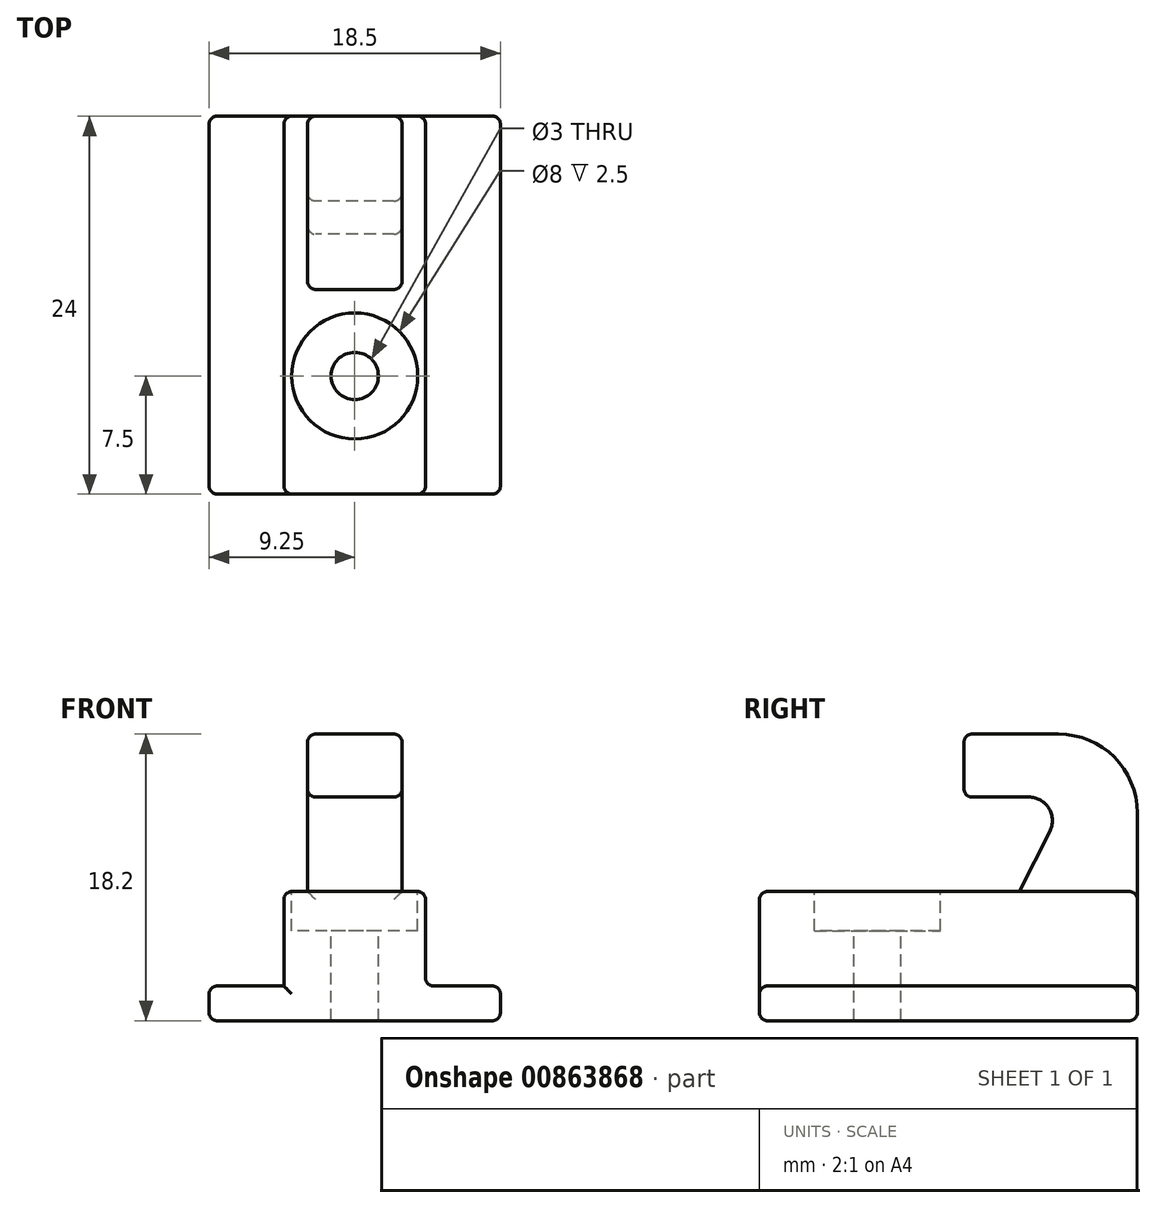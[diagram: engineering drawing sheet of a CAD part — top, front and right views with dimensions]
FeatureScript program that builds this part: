
annotation { "Feature Type Name" : "Feature", "Feature Type Description" : "" }
export const myFeature = defineFeature(function(context is Context, id is Id, definition is map)
    precondition{}
    {
        {
            var Q0;
            Q0=qCreatedBy(makeId("Top.planeOp"),FACE);
            var sketch = newSketch(context, id + "F0", { "sketchPlane" : qUnion([Q0])});
            skLineSegment(sketch, "E0.bottom", {"start": v(-9.25, 0) * mm, "end": v(9.25, 0) * mm});
            skLineSegment(sketch, "E0.top", {"start": v(-9.25, -24) * mm, "end": v(9.25, -24) * mm});
            skLineSegment(sketch, "E0.left", {"start": v(-9.25, 0) * mm, "end": v(-9.25, -24) * mm});
            skLineSegment(sketch, "E0.right", {"start": v(9.25, 0) * mm, "end": v(9.25, -24) * mm});
            skSolve(sketch);
        }
        {
            var Q0;
            Q0 = qSketchRegion(id + "F0", true);
            extrude(context, id + "F1", {"entities" : qUnion([Q0]), "depth" : 2.2 * mm, "offsetDistance" : 25 * mm});
        }
        {
            var Q0;
            Q0=makeQuery(id+"F1.opExtrude","CAP_FACE",FACE,{"disambiguationData":[OSD([sQuery(id+"F0.wireOp",EDGE,"E0.bottom"),sQuery(id+"F0.wireOp",EDGE,"E0.top"),sQuery(id+"F0.wireOp",EDGE,"E0.left"),sQuery(id+"F0.wireOp",EDGE,"E0.right")])],"isStart":false});
            var sketch = newSketch(context, id + "F2", { "sketchPlane" : qUnion([Q0])});
            skLineSegment(sketch, "E1.bottom", {"start": v(-4.5, 0) * mm, "end": v(4.5, 0) * mm});
            skLineSegment(sketch, "E1.top", {"start": v(-4.5, -24) * mm, "end": v(4.5, -24) * mm});
            skLineSegment(sketch, "E1.left", {"start": v(-4.5, 0) * mm, "end": v(-4.5, -24) * mm});
            skLineSegment(sketch, "E1.right", {"start": v(4.5, 0) * mm, "end": v(4.5, -24) * mm});
            skSolve(sketch);
        }
        {
            var Q0;
            Q0 = qSketchRegion(id + "F2", true);
            extrude(context, id + "F3", {"entities" : qUnion([Q0]), "operationType" : NewBodyOperationType.ADD, "depth" : 6 * mm, "offsetDistance" : 25 * mm});
        }
        {
            var Q0;
            Q0=qCreatedBy(makeId("Right.planeOp"),FACE);
            var sketch = newSketch(context, id + "F4", { "sketchPlane" : qUnion([Q0])});
            skLineSegment(sketch, "E2", {"start": v(-7.5, 8.2) * mm, "end": v(0, 8.2) * mm});
            skLineSegment(sketch, "E3", {"start": v(0, 8.2) * mm, "end": v(0, 17.51) * mm});
            skArc(sketch, "E4", {"start": v(0, 13.2) * mm, "mid": v(-1.46, 16.74) * mm, "end": v(-5, 18.2) * mm});
            skLineSegment(sketch, "E5", {"start": v(-7.5, 8.2) * mm, "end": v(-5.55, 12.02) * mm});
            skArc(sketch, "E6", {"start": v(-5.55, 12.02) * mm, "mid": v(-5.61, 13.48) * mm, "end": v(-6.9, 14.2) * mm});
            skLineSegment(sketch, "E7", {"start": v(-5, 18.58) * mm, "end": v(-5, 10.04) * mm, "construction": true});
            skLineSegment(sketch, "E8", {"start": v(-4.44, 18.2) * mm, "end": v(-10.5, 18.2) * mm});
            skLineSegment(sketch, "E9", {"start": v(-11, 17.7) * mm, "end": v(-11, 14.7) * mm});
            skLineSegment(sketch, "E10", {"start": v(-10.5, 14.2) * mm, "end": v(-6.9, 14.2) * mm});
            skPoint(sketch, "E11.visualSharp", {"position": v(-11, 18.2) * mm});
            skArc(sketch, "E11.filletArc", {"start": v(-10.5, 18.2) * mm, "mid": v(-10.85, 18.05) * mm, "end": v(-11, 17.7) * mm});
            skPoint(sketch, "E12.visualSharp", {"position": v(-11, 14.2) * mm});
            skArc(sketch, "E12.filletArc", {"start": v(-11, 14.7) * mm, "mid": v(-10.85, 14.35) * mm, "end": v(-10.5, 14.2) * mm});
            skSolve(sketch);
        }
        {
            var Q0;
            Q0 = qSketchRegion(id + "F4", true);
            extrude(context, id + "F5", {"entities" : qUnion([Q0]), "operationType" : NewBodyOperationType.ADD, "depth" : 3 * mm, "offsetDistance" : 25 * mm, "hasSecondDirection" : true, "secondDirectionOppositeDirection" : true, "secondDirectionDepth" : 3 * mm});
        }
        {
            var Q0;
            Q0=makeQuery(id+"F3.opExtrude","CAP_FACE",FACE,{"disambiguationData":[OSD([sQuery(id+"F2.wireOp",EDGE,"E1.bottom"),sQuery(id+"F2.wireOp",EDGE,"E1.top"),sQuery(id+"F2.wireOp",EDGE,"E1.left"),sQuery(id+"F2.wireOp",EDGE,"E1.right")])],"isStart":false});
            var sketch = newSketch(context, id + "F6", { "sketchPlane" : qUnion([Q0])});
            skPoint(sketch, "E13", {"position": v(0, -16.5) * mm});
            skSolve(sketch);
        }
        {
            var Q0;
            Q0=sQuery(id+"F6.wireOp",VERTEX,"E13");
            var Q1;
            Q1=makeQuery(id+"F1.opExtrude","SWEPT_BODY",BODY,{"disambiguationData":[OSD([sQuery(id+"F0.wireOp",EDGE,"E0.bottom"),sQuery(id+"F0.wireOp",EDGE,"E0.top"),sQuery(id+"F0.wireOp",EDGE,"E0.left"),sQuery(id+"F0.wireOp",EDGE,"E0.right")])]});
            hole(context, id + "F7", {"style" : HoleStyle.C_BORE, "endStyle" : HoleEndStyle.BLIND, "holeDiameter" : 3 * mm, "cBoreDiameter" : 8 * mm, "cBoreDepth" : 2.5 * mm, "majorDiameter" : 5 * mm, "holeDepth" : 15 * mm, "isTappedThrough" : true, "tappedDepth" : 12 * mm, "tapClearance" : 3, "startFromSketch" : true, "locations" : qUnion([Q0]), "scope" : qUnion([Q1])});
        }
        {
            var Q0;
            Q0=makeQuery(id+"F3.opExtrude","SWEPT_EDGE",EDGE,{"disambiguationData":[OSD([sQuery(id+"F0.wireOp",EDGE,"E0.top"),sQuery(id+"F2.wireOp",EDGE,"E1.top"),sQuery(id+"F2.wireOp",EDGE,"E1.left")])]});
            var Q1;
            Q1=makeQuery(id+"F1.opExtrude","SWEPT_EDGE",EDGE,{"disambiguationData":[OSD([sQuery(id+"F0.wireOp",EDGE,"E0.top"),sQuery(id+"F0.wireOp",EDGE,"E0.right")])]});
            var Q2;
            Q2=makeQuery(id+"F1.opExtrude","CAP_EDGE",EDGE,{"disambiguationData":[OSD([sQuery(id+"F0.wireOp",EDGE,"E0.left")])],"isStart":true});
            var Q3;
            Q3=makeQuery(id+"F1.opExtrude","CAP_EDGE",EDGE,{"disambiguationData":[OSD([sQuery(id+"F0.wireOp",EDGE,"E0.left")])],"isStart":false});
            var Q4;
            Q4=makeQuery(id+"F1.opExtrude","CAP_EDGE",EDGE,{"disambiguationData":[OSD([sQuery(id+"F0.wireOp",EDGE,"E0.right")])],"isStart":false});
            var Q5;
            Q5=makeQuery(id+"F3.opExtrude","SWEPT_EDGE",EDGE,{"disambiguationData":[OSD([sQuery(id+"F0.wireOp",EDGE,"E0.top"),sQuery(id+"F2.wireOp",EDGE,"E1.top"),sQuery(id+"F2.wireOp",EDGE,"E1.right")])]});
            var Q6;
            Q6=makeQuery(id+"F3.opExtrude","CAP_EDGE",EDGE,{"disambiguationData":[OSD([sQuery(id+"F2.wireOp",EDGE,"E1.top")])],"isStart":false});
            var Q7;
            Q7=makeQuery(id+"F3.opExtrude","CAP_EDGE",EDGE,{"disambiguationData":[OSD([sQuery(id+"F2.wireOp",EDGE,"E1.left")])],"isStart":false});
            var Q8;
            Q8=makeQuery(id+"F3.opExtrude","CAP_EDGE",EDGE,{"disambiguationData":[OSD([sQuery(id+"F2.wireOp",EDGE,"E1.right")])],"isStart":false});
            var Q9;
            Q9=makeQuery(id+"F3.opExtrude","CAP_EDGE",EDGE,{"disambiguationData":[OSD([sQuery(id+"F2.wireOp",EDGE,"E1.left")])],"isStart":true});
            var Q10;
            {var subQ0=sQuery(id+"F0.wireOp",EDGE,"E0.left");var subQ1=sQuery(id+"F0.wireOp",EDGE,"E0.bottom");Q10=makeQuery(id+"F3.boolean.opBoolean","SPLIT",EDGE,{"disambiguationData":[TD([makeQuery(id+"F1.opExtrude","SWEPT_FACE",FACE,{"disambiguationData":[OSD([subQ0])]})])],"derivedFrom":makeQuery(id+"F1.opExtrude","CAP_EDGE",EDGE,{"disambiguationData":[OSD([subQ1])],"isStart":false})});}
            var Q11;
            {var subQ0=sQuery(id+"F0.wireOp",EDGE,"E0.left");var subQ1=sQuery(id+"F0.wireOp",EDGE,"E0.top");Q11=makeQuery(id+"F3.boolean.opBoolean","SPLIT",EDGE,{"disambiguationData":[TD([makeQuery(id+"F1.opExtrude","SWEPT_FACE",FACE,{"disambiguationData":[OSD([subQ0])]})])],"derivedFrom":makeQuery(id+"F1.opExtrude","CAP_EDGE",EDGE,{"disambiguationData":[OSD([subQ1])],"isStart":false})});}
            var Q12;
            Q12=makeQuery(id+"F5.opExtrude","CAP_EDGE",EDGE,{"disambiguationData":[OSD([sQuery(id+"F4.wireOp",EDGE,"E4")])],"isStart":true});
            var Q13;
            Q13=makeQuery(id+"F5.opExtrude","CAP_EDGE",EDGE,{"disambiguationData":[OSD([sQuery(id+"F4.wireOp",EDGE,"E4")])],"isStart":false});
            var Q14;
            Q14=makeQuery(id+"F5.opExtrude","SWEPT_EDGE",EDGE,{"disambiguationData":[OSD([sQuery(id+"F4.wireOp",EDGE,"E2"),sQuery(id+"F4.wireOp",EDGE,"E5")])]});
            var Q15;
            Q15=makeQuery(id+"F5.opExtrude","CAP_EDGE",EDGE,{"disambiguationData":[OSD([sQuery(id+"F4.wireOp",EDGE,"E2")])],"isStart":true});
            var Q16;
            Q16=makeQuery(id+"F5.opExtrude","CAP_EDGE",EDGE,{"disambiguationData":[OSD([sQuery(id+"F4.wireOp",EDGE,"E5")])],"isStart":true});
            var Q17;
            Q17=makeQuery(id+"F5.opExtrude","CAP_EDGE",EDGE,{"disambiguationData":[OSD([sQuery(id+"F4.wireOp",EDGE,"E5")])],"isStart":false});
            var Q18;
            Q18=makeQuery(id+"F5.opExtrude","CAP_EDGE",EDGE,{"disambiguationData":[OSD([sQuery(id+"F4.wireOp",EDGE,"E6")])],"isStart":true});
            var Q19;
            Q19=makeQuery(id+"F5.opExtrude","CAP_EDGE",EDGE,{"disambiguationData":[OSD([sQuery(id+"F4.wireOp",EDGE,"E8")])],"isStart":true});
            var Q20;
            Q20=makeQuery(id+"F5.opExtrude","CAP_EDGE",EDGE,{"disambiguationData":[OSD([sQuery(id+"F4.wireOp",EDGE,"E8")])],"isStart":false});
            var Q21;
            Q21=makeQuery(id+"F5.opExtrude","CAP_EDGE",EDGE,{"disambiguationData":[OSD([sQuery(id+"F4.wireOp",EDGE,"E11.filletArc")])],"isStart":true});
            var Q22;
            Q22=makeQuery(id+"F5.opExtrude","CAP_EDGE",EDGE,{"disambiguationData":[OSD([sQuery(id+"F4.wireOp",EDGE,"E11.filletArc")])],"isStart":false});
            var Q23;
            Q23=makeQuery(id+"F7.hole-0.boolean.opBoolean","COPY",EDGE,{"derivedFrom":makeQuery(id+"F7.hole-0.opRevolve","SWEPT_EDGE",EDGE,{"disambiguationData":[OSD([sQuery(id+"F7.hole-0.sketch.wireOp",EDGE,"cbore_start_line_1"),sQuery(id+"F7.hole-0.sketch.wireOp",EDGE,"cbore_start_line_2")])]})});
            var Q24;
            Q24=makeQuery(id+"F7.hole-0.boolean.opBoolean","COPY",EDGE,{"derivedFrom":makeQuery(id+"F7.hole-0.opRevolve","SWEPT_EDGE",EDGE,{"disambiguationData":[OSD([sQuery(id+"F7.hole-0.sketch.wireOp",EDGE,"cbore_start_line_2"),sQuery(id+"F7.hole-0.sketch.wireOp",EDGE,"cbore_start_line_3")])]})});
            var Q25;
            Q25=makeQuery(id+"F7.hole-0.boolean.opBoolean","COPY",EDGE,{"derivedFrom":makeQuery(id+"F7.hole-0.opRevolve","SWEPT_EDGE",EDGE,{"disambiguationData":[OSD([sQuery(id+"F7.hole-0.sketch.wireOp",EDGE,"cbore_start_line_1"),sQuery(id+"F7.hole-0.sketch.wireOp",EDGE,"core_line_2")])]})});
            var Q26;
            Q26=makeQuery(id+"F1.opExtrude","SWEPT_EDGE",EDGE,{"disambiguationData":[OSD([sQuery(id+"F0.wireOp",EDGE,"E0.bottom"),sQuery(id+"F0.wireOp",EDGE,"E0.left")])]});
            var Q27;
            Q27=makeQuery(id+"F1.opExtrude","SWEPT_EDGE",EDGE,{"disambiguationData":[OSD([sQuery(id+"F0.wireOp",EDGE,"E0.bottom"),sQuery(id+"F0.wireOp",EDGE,"E0.right")])]});
            var Q28;
            Q28=makeQuery(id+"F7.hole-0.boolean.opBoolean","INTERSECT",EDGE,{"derivedFrom":[makeQuery(id+"F1.opExtrude","CAP_FACE",FACE,{"disambiguationData":[OSD([sQuery(id+"F0.wireOp",EDGE,"E0.bottom"),sQuery(id+"F0.wireOp",EDGE,"E0.top"),sQuery(id+"F0.wireOp",EDGE,"E0.left"),sQuery(id+"F0.wireOp",EDGE,"E0.right")])],"isStart":true}),makeQuery(id+"F7.hole-0.opRevolve","SWEPT_FACE",FACE,{"disambiguationData":[OSD([sQuery(id+"F7.hole-0.sketch.wireOp",EDGE,"core_line_2")])]})]});
            var Q29;
            Q29=makeQuery(id+"F1.opExtrude","SWEPT_EDGE",EDGE,{"disambiguationData":[OSD([sQuery(id+"F0.wireOp",EDGE,"E0.top"),sQuery(id+"F0.wireOp",EDGE,"E0.left")])]});
            var Q30;
            Q30=makeQuery(id+"F3.opExtrude","SWEPT_EDGE",EDGE,{"disambiguationData":[OSD([sQuery(id+"F0.wireOp",EDGE,"E0.bottom"),sQuery(id+"F2.wireOp",EDGE,"E1.bottom"),sQuery(id+"F2.wireOp",EDGE,"E1.right")])]});
            var Q31;
            Q31=makeQuery(id+"F1.opExtrude","CAP_EDGE",EDGE,{"disambiguationData":[OSD([sQuery(id+"F0.wireOp",EDGE,"E0.bottom")])],"isStart":true});
            var Q32;
            Q32=makeQuery(id+"F3.opExtrude","SWEPT_EDGE",EDGE,{"disambiguationData":[OSD([sQuery(id+"F0.wireOp",EDGE,"E0.bottom"),sQuery(id+"F2.wireOp",EDGE,"E1.bottom"),sQuery(id+"F2.wireOp",EDGE,"E1.left")])]});
            var Q33;
            Q33=makeQuery(id+"F1.opExtrude","CAP_EDGE",EDGE,{"disambiguationData":[OSD([sQuery(id+"F0.wireOp",EDGE,"E0.top")])],"isStart":true});
            var Q34;
            Q34=makeQuery(id+"F1.opExtrude","CAP_EDGE",EDGE,{"disambiguationData":[OSD([sQuery(id+"F0.wireOp",EDGE,"E0.right")])],"isStart":true});
            var Q35;
            Q35=makeQuery(id+"F5.opExtrude","CAP_EDGE",EDGE,{"disambiguationData":[OSD([sQuery(id+"F4.wireOp",EDGE,"E3")])],"isStart":false});
            var Q36;
            Q36=makeQuery(id+"F3.opExtrude","CAP_EDGE",EDGE,{"disambiguationData":[OSD([sQuery(id+"F2.wireOp",EDGE,"E1.right")])],"isStart":true});
            var Q37;
            {var subQ0=sQuery(id+"F0.wireOp",EDGE,"E0.right");var subQ1=sQuery(id+"F0.wireOp",EDGE,"E0.bottom");Q37=makeQuery(id+"F3.boolean.opBoolean","SPLIT",EDGE,{"disambiguationData":[TD([makeQuery(id+"F1.opExtrude","SWEPT_FACE",FACE,{"disambiguationData":[OSD([subQ0])]})])],"derivedFrom":makeQuery(id+"F1.opExtrude","CAP_EDGE",EDGE,{"disambiguationData":[OSD([subQ1])],"isStart":false})});}
            var Q38;
            {var subQ0=sQuery(id+"F0.wireOp",EDGE,"E0.right");var subQ1=sQuery(id+"F0.wireOp",EDGE,"E0.top");Q38=makeQuery(id+"F3.boolean.opBoolean","SPLIT",EDGE,{"disambiguationData":[TD([makeQuery(id+"F1.opExtrude","SWEPT_FACE",FACE,{"disambiguationData":[OSD([subQ0])]})])],"derivedFrom":makeQuery(id+"F1.opExtrude","CAP_EDGE",EDGE,{"disambiguationData":[OSD([subQ1])],"isStart":false})});}
            var Q39;
            Q39=makeQuery(id+"F5.opExtrude","SWEPT_EDGE",EDGE,{"disambiguationData":[OSD([sQuery(id+"F4.wireOp",EDGE,"E3"),sQuery(id+"F4.wireOp",EDGE,"E4")])]});
            var Q40;
            Q40=makeQuery(id+"F5.opExtrude","SWEPT_EDGE",EDGE,{"disambiguationData":[OSD([sQuery(id+"F4.wireOp",EDGE,"E4"),sQuery(id+"F4.wireOp",EDGE,"E8")])]});
            var Q41;
            Q41=makeQuery(id+"F5.opExtrude","SWEPT_EDGE",EDGE,{"disambiguationData":[OSD([sQuery(id+"F4.wireOp",EDGE,"E5"),sQuery(id+"F4.wireOp",EDGE,"E6")])]});
            var Q42;
            Q42=makeQuery(id+"F5.opExtrude","SWEPT_EDGE",EDGE,{"disambiguationData":[OSD([sQuery(id+"F4.wireOp",EDGE,"E6"),sQuery(id+"F4.wireOp",EDGE,"E10")])]});
            var Q43;
            Q43=makeQuery(id+"F5.opExtrude","SWEPT_EDGE",EDGE,{"disambiguationData":[OSD([sQuery(id+"F4.wireOp",EDGE,"E8"),sQuery(id+"F4.wireOp",EDGE,"E11.filletArc")])]});
            var Q44;
            Q44=makeQuery(id+"F5.opExtrude","SWEPT_EDGE",EDGE,{"disambiguationData":[OSD([sQuery(id+"F4.wireOp",EDGE,"E9"),sQuery(id+"F4.wireOp",EDGE,"E11.filletArc")])]});
            var Q45;
            Q45=makeQuery(id+"F5.opExtrude","SWEPT_EDGE",EDGE,{"disambiguationData":[OSD([sQuery(id+"F4.wireOp",EDGE,"E9"),sQuery(id+"F4.wireOp",EDGE,"E12.filletArc")])]});
            var Q46;
            Q46=makeQuery(id+"F5.opExtrude","SWEPT_EDGE",EDGE,{"disambiguationData":[OSD([sQuery(id+"F4.wireOp",EDGE,"E10"),sQuery(id+"F4.wireOp",EDGE,"E12.filletArc")])]});
            var Q47;
            Q47=makeQuery(id+"F5.opExtrude","CAP_EDGE",EDGE,{"disambiguationData":[OSD([sQuery(id+"F4.wireOp",EDGE,"E3")])],"isStart":true});
            var Q48;
            Q48=makeQuery(id+"F5.opExtrude","CAP_EDGE",EDGE,{"disambiguationData":[OSD([sQuery(id+"F4.wireOp",EDGE,"E2")])],"isStart":false});
            var Q49;
            {var subQ0=sQuery(id+"F2.wireOp",EDGE,"E1.left");var subQ1=sQuery(id+"F2.wireOp",EDGE,"E1.bottom");Q49=makeQuery(id+"F5.boolean.opBoolean","SPLIT",EDGE,{"disambiguationData":[TD([makeQuery(id+"F3.opExtrude","SWEPT_FACE",FACE,{"disambiguationData":[OSD([subQ0])]})])],"derivedFrom":makeQuery(id+"F3.opExtrude","CAP_EDGE",EDGE,{"disambiguationData":[OSD([subQ1])],"isStart":false})});}
            var Q50;
            {var subQ0=sQuery(id+"F2.wireOp",EDGE,"E1.right");var subQ1=sQuery(id+"F2.wireOp",EDGE,"E1.bottom");Q50=makeQuery(id+"F5.boolean.opBoolean","SPLIT",EDGE,{"disambiguationData":[TD([makeQuery(id+"F3.opExtrude","SWEPT_FACE",FACE,{"disambiguationData":[OSD([subQ0])]})])],"derivedFrom":makeQuery(id+"F3.opExtrude","CAP_EDGE",EDGE,{"disambiguationData":[OSD([subQ1])],"isStart":false})});}
            var Q51;
            Q51=makeQuery(id+"F5.opExtrude","CAP_EDGE",EDGE,{"disambiguationData":[OSD([sQuery(id+"F4.wireOp",EDGE,"E6")])],"isStart":false});
            var Q52;
            Q52=makeQuery(id+"F5.opExtrude","CAP_EDGE",EDGE,{"disambiguationData":[OSD([sQuery(id+"F4.wireOp",EDGE,"E9")])],"isStart":true});
            var Q53;
            Q53=makeQuery(id+"F5.opExtrude","CAP_EDGE",EDGE,{"disambiguationData":[OSD([sQuery(id+"F4.wireOp",EDGE,"E9")])],"isStart":false});
            var Q54;
            Q54=makeQuery(id+"F5.opExtrude","CAP_EDGE",EDGE,{"disambiguationData":[OSD([sQuery(id+"F4.wireOp",EDGE,"E10")])],"isStart":true});
            var Q55;
            Q55=makeQuery(id+"F5.opExtrude","CAP_EDGE",EDGE,{"disambiguationData":[OSD([sQuery(id+"F4.wireOp",EDGE,"E10")])],"isStart":false});
            var Q56;
            Q56=makeQuery(id+"F5.opExtrude","CAP_EDGE",EDGE,{"disambiguationData":[OSD([sQuery(id+"F4.wireOp",EDGE,"E12.filletArc")])],"isStart":true});
            var Q57;
            Q57=makeQuery(id+"F5.opExtrude","CAP_EDGE",EDGE,{"disambiguationData":[OSD([sQuery(id+"F4.wireOp",EDGE,"E12.filletArc")])],"isStart":false});
            fillet(context, id + "F8", {"entities" : qUnion([Q0, Q1, Q2, Q3, Q4, Q5, Q6, Q7, Q8, Q9, Q10, Q11, Q12, Q13, Q14, Q15, Q16, Q17, Q18, Q19, Q20, Q21, Q22, Q23, Q24, Q25, Q26, Q27, Q28, Q29, Q30, Q31, Q32, Q33, Q34, Q35, Q36, Q37, Q38, Q39, Q40, Q41, Q42, Q43, Q44, Q45, Q46, Q47, Q48, Q49, Q50, Q51, Q52, Q53, Q54, Q55, Q56, Q57]), "radius" : 0.5 * mm, "tangentPropagation" : true, "allowEdgeOverflow" : false});
        }
    });
